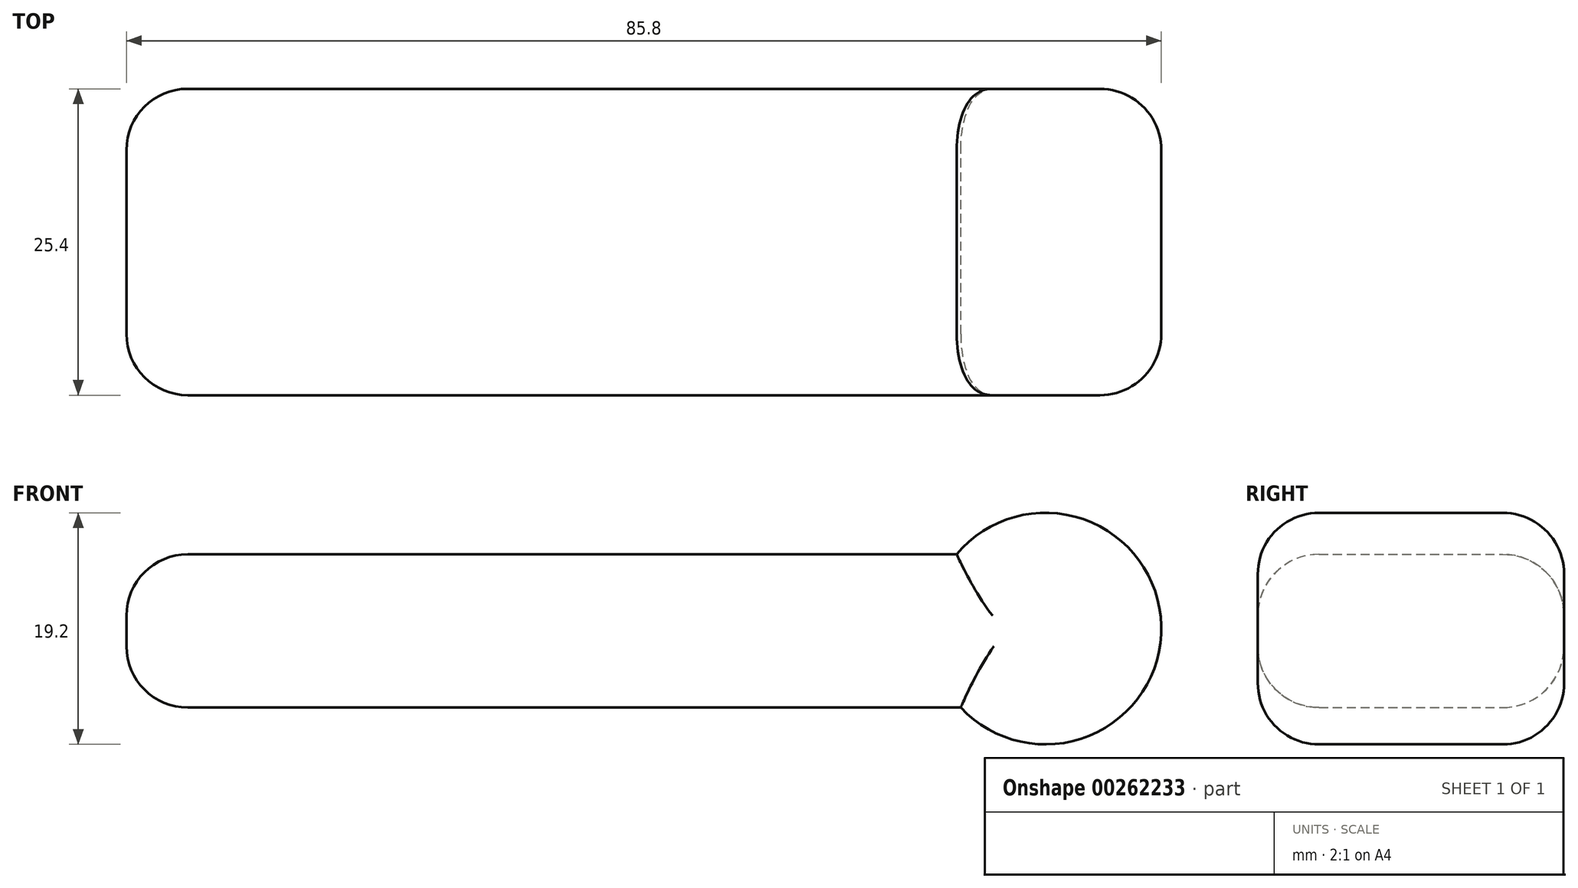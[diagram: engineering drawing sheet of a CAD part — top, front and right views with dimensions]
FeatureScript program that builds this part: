
annotation { "Feature Type Name" : "Feature", "Feature Type Description" : "" }
export const myFeature = defineFeature(function(context is Context, id is Id, definition is map)
    precondition{}
    {
        {
            var Q0;
            Q0=qCreatedBy(makeId("Front.planeOp"),FACE);
            var sketch = newSketch(context, id + "F0", { "sketchPlane" : qUnion([Q0])});
            skLineSegment(sketch, "E0", {"start": v(0, 6.16) * mm, "end": v(-76.2, 6.16) * mm});
            skLineSegment(sketch, "E1", {"start": v(-76.2, 6.16) * mm, "end": v(-76.2, -6.54) * mm});
            skLineSegment(sketch, "E2", {"start": v(-76.2, -6.54) * mm, "end": v(0, -6.54) * mm});
            skLineSegment(sketch, "E3", {"start": v(0, -6.54) * mm, "end": v(0, 6.16) * mm});
            skCircle(sketch, "E4", {"center": v(0, 0) * mm, "radius": 9.6 * mm});
            skSolve(sketch);
        }
        {
            var Q0;
            {var subQ0=sQuery(id+"F0.wireOp",EDGE,"E1");Q0=makeQuery(id+"F0.imprint","IMPRINT",FACE,{"disambiguationData":[TD([[makeQuery(id+"F0.imprint","IMPRINT",EDGE,{"derivedFrom":subQ0}),1.0]])]});}
            var Q1;
            {var subQ0=sQuery(id+"F0.wireOp",EDGE,"E3");Q1=makeQuery(id+"F0.imprint","IMPRINT",FACE,{"disambiguationData":[TD([[makeQuery(id+"F0.imprint","IMPRINT",EDGE,{"derivedFrom":subQ0}),1.0]])]});}
            var Q2;
            {var subQ0=sQuery(id+"F0.wireOp",EDGE,"E3");Q2=makeQuery(id+"F0.imprint","IMPRINT",FACE,{"disambiguationData":[TD([[makeQuery(id+"F0.imprint","IMPRINT",EDGE,{"derivedFrom":subQ0}),-1.0]])]});}
            extrude(context, id + "F1", {"entities" : qUnion([Q0, Q1, Q2]), "depth" : 25.4 * mm});
        }
        {
            var Q0;
            Q0=makeQuery(id+"F1.opExtrude","CAP_EDGE",EDGE,{"disambiguationData":[OSD([sQuery(id+"F0.wireOp",EDGE,"E1")])],"isStart":false});
            var Q1;
            Q1=makeQuery(id+"F1.opExtrude","SWEPT_FACE",FACE,{"disambiguationData":[OSD([sQuery(id+"F0.wireOp",EDGE,"E1")])]});
            var Q2;
            Q2=makeQuery(id+"F1.opExtrude","CAP_EDGE",EDGE,{"disambiguationData":[OSD([sQuery(id+"F0.wireOp",EDGE,"E0")])],"isStart":true});
            var Q3;
            Q3=makeQuery(id+"F1.opExtrude","CAP_EDGE",EDGE,{"disambiguationData":[OSD([sQuery(id+"F0.wireOp",EDGE,"E2")])],"isStart":true});
            var Q4;
            Q4=makeQuery(id+"F1.opExtrude","CAP_EDGE",EDGE,{"disambiguationData":[OSD([sQuery(id+"F0.wireOp",EDGE,"E0")])],"isStart":false});
            var Q5;
            Q5=makeQuery(id+"F1.opExtrude","CAP_EDGE",EDGE,{"disambiguationData":[OSD([sQuery(id+"F0.wireOp",EDGE,"E2")])],"isStart":false});
            fillet(context, id + "F2", {"entities" : qUnion([Q0, Q1, Q2, Q3, Q4, Q5]), "radius" : 5.08 * mm, "tangentPropagation" : true, "allowEdgeOverflow" : false});
        }
        {
            var Q0;
            Q0=makeQuery(id+"F1.opExtrude","CAP_EDGE",EDGE,{"disambiguationData":[OSD([sQuery(id+"F0.wireOp",EDGE,"E4")])],"isStart":false});
            var Q1;
            Q1=makeQuery(id+"F1.opExtrude","CAP_EDGE",EDGE,{"disambiguationData":[OSD([sQuery(id+"F0.wireOp",EDGE,"E4")])],"isStart":true});
            fillet(context, id + "F3", {"entities" : qUnion([Q0, Q1]), "radius" : 5.08 * mm, "tangentPropagation" : true, "allowEdgeOverflow" : false});
        }
    });
